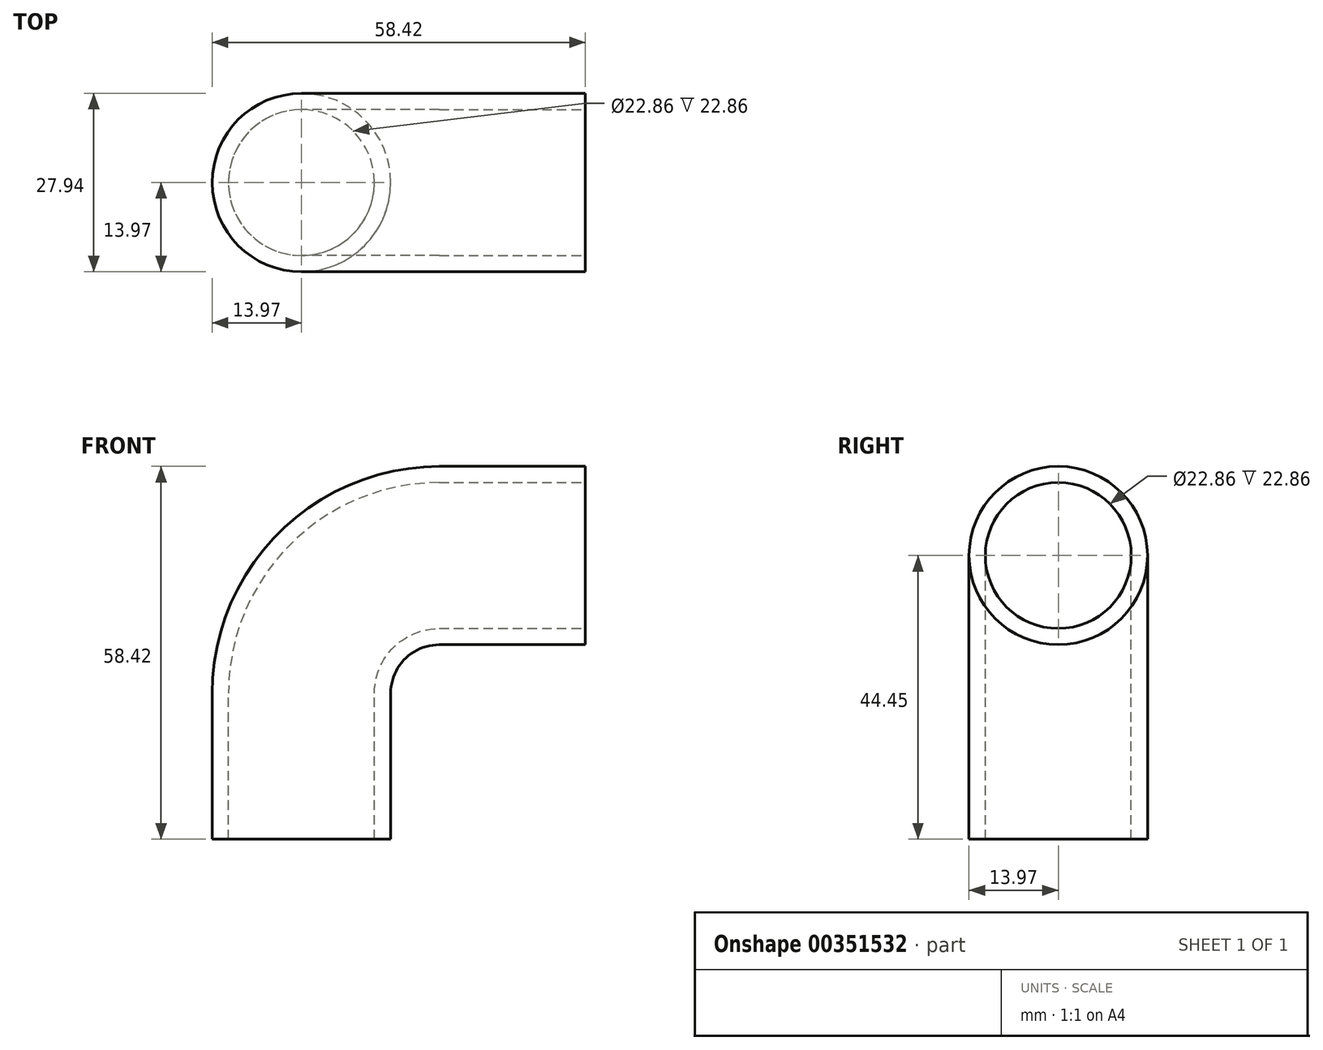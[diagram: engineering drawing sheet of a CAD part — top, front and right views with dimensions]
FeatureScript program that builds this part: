
annotation { "Feature Type Name" : "Feature", "Feature Type Description" : "" }
export const myFeature = defineFeature(function(context is Context, id is Id, definition is map)
    precondition{}
    {
        {
            var Q0;
            Q0=qCreatedBy(makeId("Top.planeOp"),FACE);
            var sketch = newSketch(context, id + "F0", { "sketchPlane" : qUnion([Q0])});
            skCircle(sketch, "E0", {"center": v(0, 0) * mm, "radius": 13.97 * mm});
            skCircle(sketch, "E1", {"center": v(0, 0) * mm, "radius": 11.43 * mm});
            skSolve(sketch);
        }
        {
            var Q0;
            Q0=qCreatedBy(makeId("Front.planeOp"),FACE);
            var sketch = newSketch(context, id + "F1", { "sketchPlane" : qUnion([Q0])});
            skLineSegment(sketch, "E2", {"start": v(0, 0) * mm, "end": v(0, 22.86) * mm});
            skLineSegment(sketch, "E3", {"start": v(-18.37, 0) * mm, "end": v(35.67, 0) * mm, "construction": true});
            skLineSegment(sketch, "E4", {"start": v(-27.61, 44.45) * mm, "end": v(30.23, 44.45) * mm, "construction": true});
            skLineSegment(sketch, "E5", {"start": v(44.45, 54.3) * mm, "end": v(44.45, 0) * mm, "construction": true});
            skLineSegment(sketch, "E6", {"start": v(44.45, 44.45) * mm, "end": v(21.59, 44.45) * mm});
            skArc(sketch, "E7", {"start": v(0, 22.86) * mm, "mid": v(6.32, 38.13) * mm, "end": v(21.6, 44.45) * mm});
            skSolve(sketch);
        }
        {
            var Q0;
            Q0=makeQuery(id+"F0.imprint","IMPRINT",FACE,{"disambiguationData":[TD([[makeQuery(id+"F0.imprint","IMPRINT",EDGE,{"derivedFrom":sQuery(id+"F0.wireOp",EDGE,"E0")}),1.0]])]});
            var Q1;
            Q1 = qConstructionFilter(qBodyType(qCreatedBy(id + "F1" ,EDGE), BodyType.WIRE), ConstructionObject.NO);
            sweep(context, id + "F2", {"profiles" : qUnion([Q0]), "path" : qUnion([Q1])});
        }
    });
